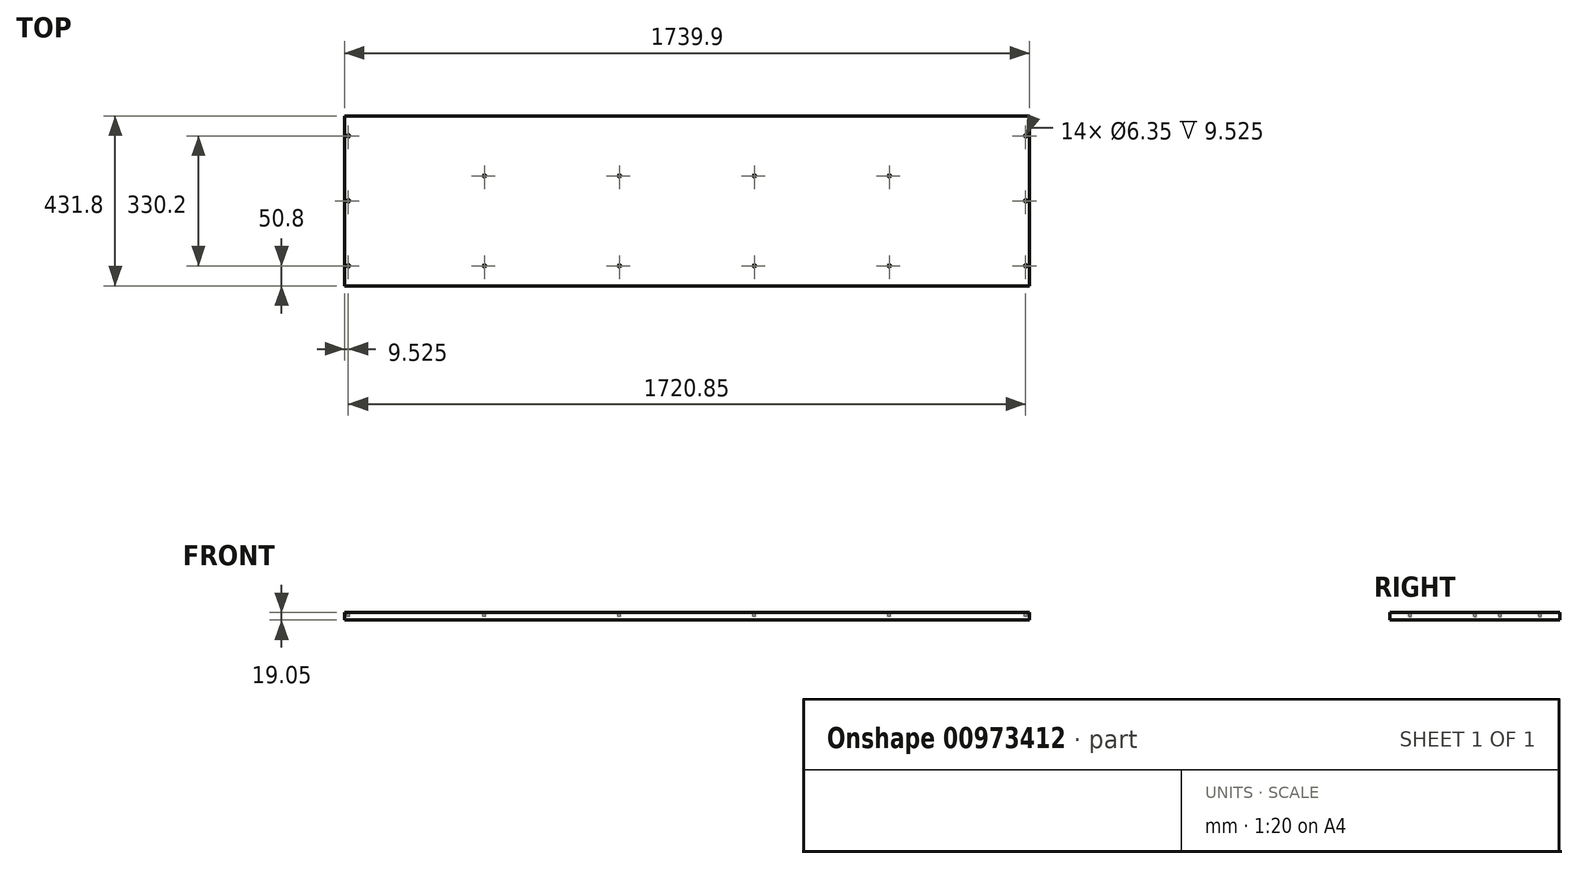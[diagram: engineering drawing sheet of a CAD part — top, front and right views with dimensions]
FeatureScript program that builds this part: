
annotation { "Feature Type Name" : "Feature", "Feature Type Description" : "" }
export const myFeature = defineFeature(function(context is Context, id is Id, definition is map)
    precondition{}
    {
        {
            var Q0;
            Q0=qCreatedBy(makeId("Front.planeOp"),FACE);
            var sketch = newSketch(context, id + "F0", { "sketchPlane" : qUnion([Q0])});
            skLineSegment(sketch, "E0.bottom", {"start": v(0, 19.05) * mm, "end": v(1739.9, 19.05) * mm});
            skLineSegment(sketch, "E0.top", {"start": v(0, 0) * mm, "end": v(1739.9, 0) * mm});
            skLineSegment(sketch, "E0.left", {"start": v(0, 19.05) * mm, "end": v(0, 0) * mm});
            skLineSegment(sketch, "E0.right", {"start": v(1739.9, 19.05) * mm, "end": v(1739.9, 0) * mm});
            skSolve(sketch);
        }
        {
            var Q0;
            Q0 = qSketchRegion(id + "F0", true);
            extrude(context, id + "F1", {"entities" : qUnion([Q0]), "oppositeDirection" : true, "depth" : 431.8 * mm, "offsetDistance" : 25.4 * mm});
        }
        {
            var Q0;
            Q0=makeQuery(id+"F1.opExtrude","SWEPT_FACE",FACE,{"disambiguationData":[OSD([sQuery(id+"F0.wireOp",EDGE,"E0.bottom")])]});
            var sketch = newSketch(context, id + "F2", { "sketchPlane" : qUnion([Q0])});
            skCircle(sketch, "E1", {"center": v(9.53, 381) * mm, "radius": 3.18 * mm});
            skCircle(sketch, "E2", {"center": v(9.53, 215.9) * mm, "radius": 3.18 * mm});
            skCircle(sketch, "E3", {"center": v(9.53, 50.8) * mm, "radius": 3.18 * mm});
            skCircle(sketch, "E4", {"center": v(1730.38, 381) * mm, "radius": 3.18 * mm});
            skCircle(sketch, "E5", {"center": v(1730.38, 215.9) * mm, "radius": 3.18 * mm});
            skCircle(sketch, "E6", {"center": v(1730.38, 50.8) * mm, "radius": 3.18 * mm});
            skCircle(sketch, "E7", {"center": v(355.6, 50.8) * mm, "radius": 3.18 * mm});
            skCircle(sketch, "E8", {"center": v(355.6, 279.4) * mm, "radius": 3.18 * mm});
            skCircle(sketch, "E9", {"center": v(1041.4, 50.8) * mm, "radius": 3.18 * mm});
            skCircle(sketch, "E10", {"center": v(1384.3, 279.4) * mm, "radius": 3.18 * mm});
            skCircle(sketch, "E11", {"center": v(1041.4, 279.4) * mm, "radius": 3.18 * mm});
            skCircle(sketch, "E12", {"center": v(698.5, 50.8) * mm, "radius": 3.18 * mm});
            skCircle(sketch, "E13", {"center": v(698.5, 279.4) * mm, "radius": 3.18 * mm});
            skCircle(sketch, "E14", {"center": v(1384.3, 50.8) * mm, "radius": 3.18 * mm});
            skSolve(sketch);
        }
        {
            var Q0;
            Q0 = qSketchRegion(id + "F2", true);
            extrude(context, id + "F3", {"entities" : qUnion([Q0]), "operationType" : NewBodyOperationType.REMOVE, "oppositeDirection" : true, "depth" : 9.52 * mm, "offsetDistance" : 25.4 * mm});
        }
    });
